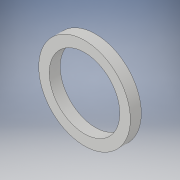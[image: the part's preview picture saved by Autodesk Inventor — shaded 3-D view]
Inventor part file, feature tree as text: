
AUTODESK INVENTOR PART (.ipt)
format: ipt  version: 2019 (Build 230136000, 136)  size: 103,936 bytes
history: native  units: mm
features: extrude x2, sketch x2
ambient origin geometry x8: Origin, YZ Plane, XZ Plane, XY Plane, X Axis, Y Axis, Z Axis, Center Point
bodies: Solid1 (feature_tree)
feature tree (4):
  extrude  "Extrusion1"  Depth=4.11mm TaperAngle=0.0deg
  extrude  "Extrusion2"  Depth=4.11mm TaperAngle=0.0deg
  sketch  "Sketch1"  dims[d0=34.4mm d1=4.11mm d2=0.0mm]
  sketch  "Sketch2"  dims[d3=26.5mm d4=4.11mm d5=0.0mm]
